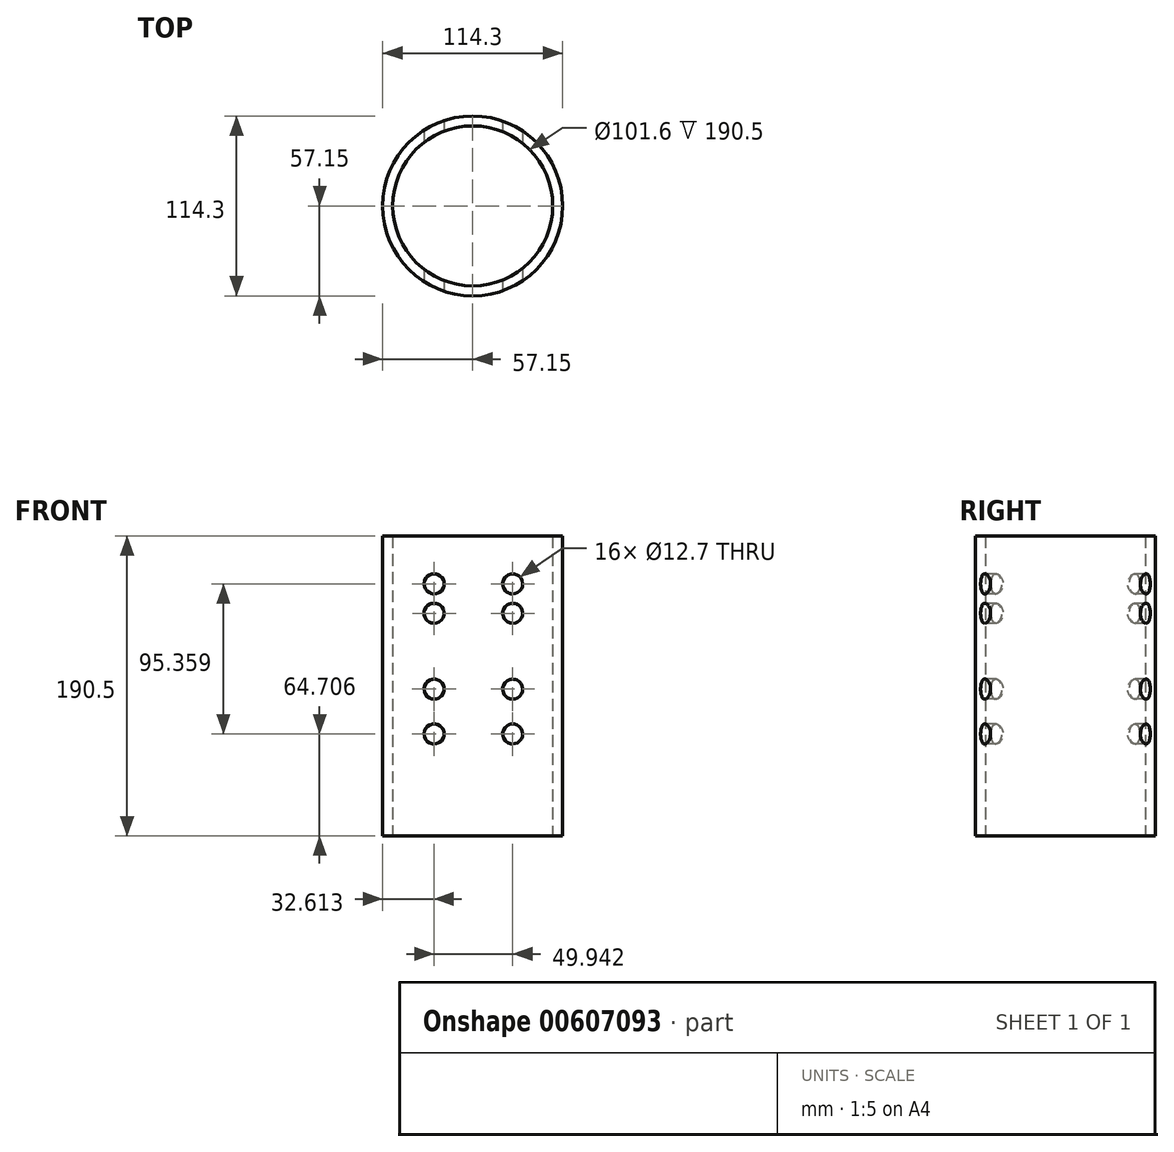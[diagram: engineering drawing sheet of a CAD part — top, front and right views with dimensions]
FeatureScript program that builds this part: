
annotation { "Feature Type Name" : "Feature", "Feature Type Description" : "" }
export const myFeature = defineFeature(function(context is Context, id is Id, definition is map)
    precondition{}
    {
        {
            var Q0;
            Q0=qCreatedBy(makeId("Top.planeOp"),FACE);
            var sketch = newSketch(context, id + "F0", { "sketchPlane" : qUnion([Q0])});
            skCircle(sketch, "E0", {"center": v(0, 0) * mm, "radius": 57.15 * mm});
            skCircle(sketch, "E1", {"center": v(0, 0) * mm, "radius": 50.8 * mm});
            skSolve(sketch);
        }
        {
            var Q0;
            Q0 = qSketchRegion(id + "F0", true);
            extrude(context, id + "F1", {"entities" : qUnion([Q0]), "depth" : 190.5 * mm, "offsetDistance" : 25.4 * mm});
        }
        {
            var Q0;
            Q0=qCreatedBy(makeId("Front.planeOp"),FACE);
            var sketch = newSketch(context, id + "F2", { "sketchPlane" : qUnion([Q0])});
            skCircle(sketch, "E2", {"center": v(25.4, 93.23) * mm, "radius": 6.35 * mm});
            skCircle(sketch, "E3", {"center": v(25.4, 160.07) * mm, "radius": 6.35 * mm});
            skCircle(sketch, "E4", {"center": v(25.4, 141.43) * mm, "radius": 6.35 * mm});
            skCircle(sketch, "E5", {"center": v(25.4, 64.7) * mm, "radius": 6.35 * mm});
            skCircle(sketch, "E6", {"center": v(-24.54, 93.23) * mm, "radius": 6.35 * mm});
            skCircle(sketch, "E7", {"center": v(-24.53, 141.43) * mm, "radius": 6.35 * mm});
            skCircle(sketch, "E8", {"center": v(-24.54, 160.07) * mm, "radius": 6.35 * mm});
            skCircle(sketch, "E9", {"center": v(-24.54, 64.77) * mm, "radius": 6.35 * mm});
            skSolve(sketch);
        }
        {
            var Q0;
            Q0=makeQuery(id+"F2.imprint","IMPRINT",FACE,{"disambiguationData":[TD([[makeQuery(id+"F2.imprint","IMPRINT",EDGE,{"derivedFrom":sQuery(id+"F2.wireOp",EDGE,"1Z29irsO-K2st-IyxM-erPI-dXm4Y1ezKJUR")}),1.0]])]});
            var Q1;
            Q1=makeQuery(id+"F2.imprint","IMPRINT",FACE,{"disambiguationData":[TD([[makeQuery(id+"F2.imprint","IMPRINT",EDGE,{"derivedFrom":sQuery(id+"F2.wireOp",EDGE,"LWckmPuU-AspG-2XR0-R6cz-vkgy2M1TDrAo")}),1.0]])]});
            var Q2;
            Q2=makeQuery(id+"F2.imprint","IMPRINT",FACE,{"disambiguationData":[TD([[makeQuery(id+"F2.imprint","IMPRINT",EDGE,{"derivedFrom":sQuery(id+"F2.wireOp",EDGE,"E2")}),1.0]])]});
            var Q3;
            Q3=makeQuery(id+"F2.imprint","IMPRINT",FACE,{"disambiguationData":[TD([[makeQuery(id+"F2.imprint","IMPRINT",EDGE,{"derivedFrom":sQuery(id+"F2.wireOp",EDGE,"E3")}),1.0]])]});
            var Q4;
            Q4=makeQuery(id+"F2.imprint","IMPRINT",FACE,{"disambiguationData":[TD([[makeQuery(id+"F2.imprint","IMPRINT",EDGE,{"derivedFrom":sQuery(id+"F2.wireOp",EDGE,"T23N0zG3-5NFY-OJzE-PyZH-g8voepTbotsx")}),1.0]])]});
            var Q5;
            Q5=makeQuery(id+"F2.imprint","IMPRINT",FACE,{"disambiguationData":[TD([[makeQuery(id+"F2.imprint","IMPRINT",EDGE,{"derivedFrom":sQuery(id+"F2.wireOp",EDGE,"E4")}),1.0]])]});
            var Q6;
            Q6=makeQuery(id+"F2.imprint","IMPRINT",FACE,{"disambiguationData":[TD([[makeQuery(id+"F2.imprint","IMPRINT",EDGE,{"derivedFrom":sQuery(id+"F2.wireOp",EDGE,"E5")}),1.0]])]});
            var Q7;
            Q7=makeQuery(id+"F2.imprint","IMPRINT",FACE,{"disambiguationData":[TD([[makeQuery(id+"F2.imprint","IMPRINT",EDGE,{"derivedFrom":sQuery(id+"F2.wireOp",EDGE,"E6")}),1.0]])]});
            var Q8;
            Q8=makeQuery(id+"F2.imprint","IMPRINT",FACE,{"disambiguationData":[TD([[makeQuery(id+"F2.imprint","IMPRINT",EDGE,{"derivedFrom":sQuery(id+"F2.wireOp",EDGE,"E7")}),1.0]])]});
            var Q9;
            Q9=makeQuery(id+"F2.imprint","IMPRINT",FACE,{"disambiguationData":[TD([[makeQuery(id+"F2.imprint","IMPRINT",EDGE,{"derivedFrom":sQuery(id+"F2.wireOp",EDGE,"E8")}),1.0]])]});
            var Q10;
            Q10=makeQuery(id+"F2.imprint","IMPRINT",FACE,{"disambiguationData":[TD([[makeQuery(id+"F2.imprint","IMPRINT",EDGE,{"derivedFrom":sQuery(id+"F2.wireOp",EDGE,"E9")}),1.0]])]});
            extrude(context, id + "F3", {"entities" : qUnion([Q0, Q1, Q2, Q3, Q4, Q5, Q6, Q7, Q8, Q9, Q10]), "operationType" : NewBodyOperationType.REMOVE, "oppositeDirection" : true, "depth" : 76.2 * mm, "offsetDistance" : 25.4 * mm, "hasSecondDirection" : true, "secondDirectionOppositeDirection" : false, "secondDirectionDepth" : 76.2 * mm});
        }
    });
